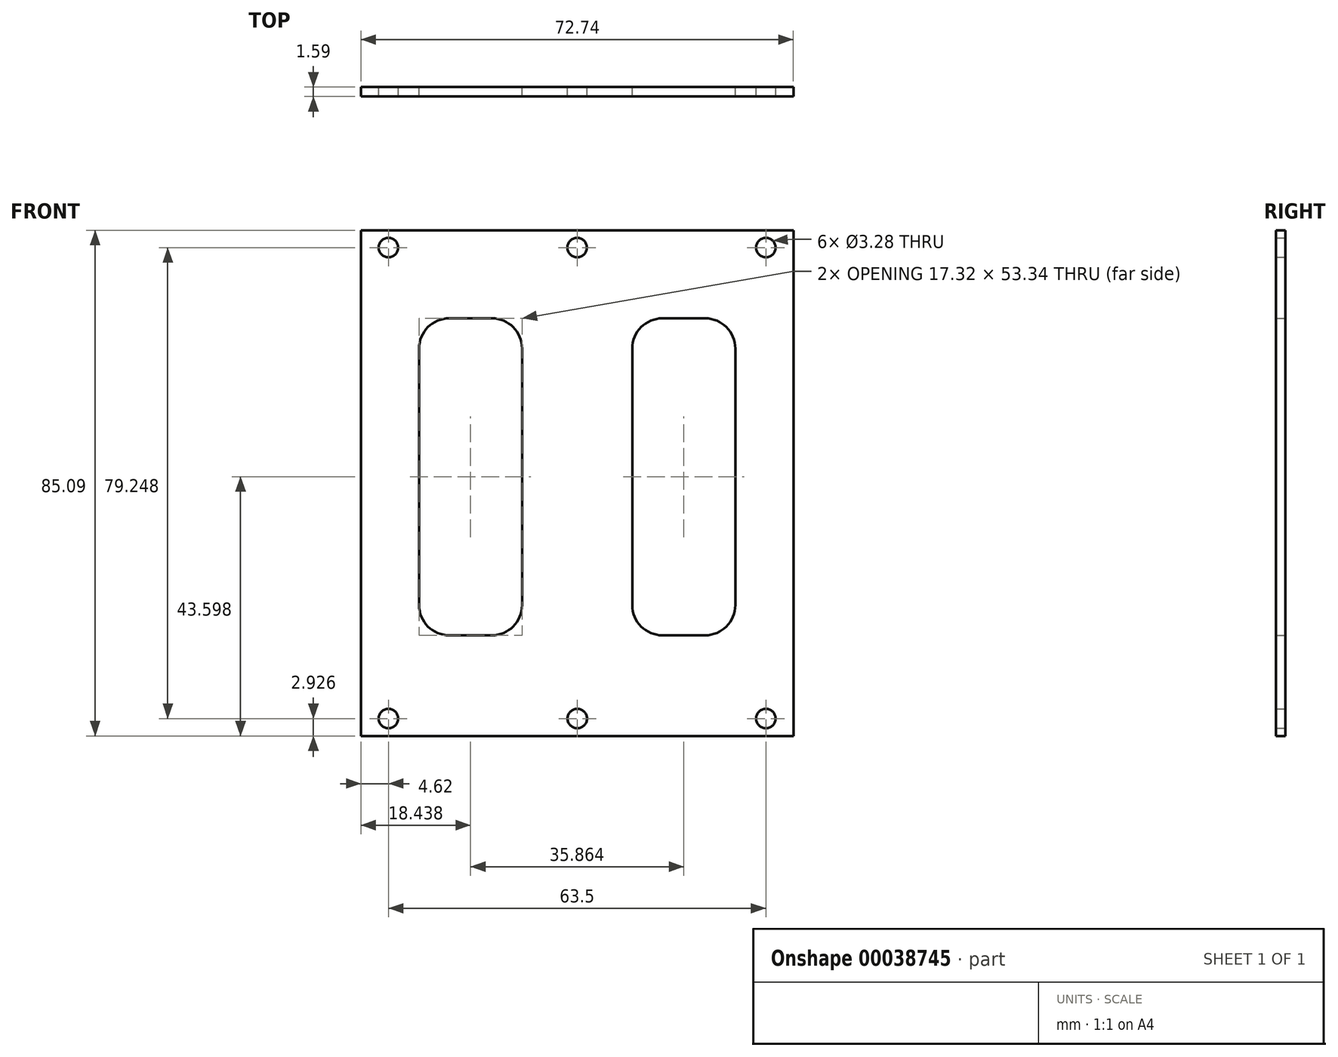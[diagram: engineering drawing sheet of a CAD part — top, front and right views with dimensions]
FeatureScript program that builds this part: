
annotation { "Feature Type Name" : "Feature", "Feature Type Description" : "" }
export const myFeature = defineFeature(function(context is Context, id is Id, definition is map)
    precondition{}
    {
        {
            var Q0;
            Q0=qCreatedBy(makeId("Front.planeOp"),FACE);
            var sketch = newSketch(context, id + "F0", { "sketchPlane" : qUnion([Q0])});
            skLineSegment(sketch, "E0.bottom", {"start": v(-36.37, 49.36) * mm, "end": v(36.37, 49.36) * mm});
            skLineSegment(sketch, "E0.top", {"start": v(-36.37, -35.73) * mm, "end": v(36.37, -35.73) * mm});
            skLineSegment(sketch, "E0.left", {"start": v(-36.37, 49.36) * mm, "end": v(-36.37, -35.73) * mm});
            skLineSegment(sketch, "E0.right", {"start": v(36.37, 49.36) * mm, "end": v(36.37, -35.73) * mm});
            skCircle(sketch, "E1", {"center": v(-31.75, 46.44) * mm, "radius": 1.64 * mm});
            skCircle(sketch, "E2", {"center": v(0, 46.44) * mm, "radius": 1.64 * mm});
            skCircle(sketch, "E3", {"center": v(31.75, 46.44) * mm, "radius": 1.64 * mm});
            skCircle(sketch, "E4", {"center": v(-31.75, -32.8) * mm, "radius": 1.64 * mm});
            skCircle(sketch, "E5", {"center": v(0.02, -32.8) * mm, "radius": 1.64 * mm});
            skCircle(sketch, "E6", {"center": v(31.75, -32.8) * mm, "radius": 1.64 * mm});
            skLineSegment(sketch, "E7", {"start": v(0, 0) * mm, "end": v(0, 63.69) * mm, "construction": true});
            skLineSegment(sketch, "E8", {"start": v(0, 0) * mm, "end": v(0, -66.16) * mm, "construction": true});
            skLineSegment(sketch, "E9.bottom", {"start": v(-26.6, 34.54) * mm, "end": v(-9.27, 34.54) * mm});
            skLineSegment(sketch, "E9.top", {"start": v(-26.6, -18.8) * mm, "end": v(-9.27, -18.8) * mm});
            skLineSegment(sketch, "E9.left", {"start": v(-26.6, 34.54) * mm, "end": v(-26.6, -18.8) * mm});
            skLineSegment(sketch, "E9.right", {"start": v(-9.27, 34.54) * mm, "end": v(-9.27, -18.8) * mm});
            skLineSegment(sketch, "E10.bottom", {"start": v(9.27, 34.54) * mm, "end": v(26.6, 34.54) * mm});
            skLineSegment(sketch, "E10.top", {"start": v(9.27, -18.8) * mm, "end": v(26.6, -18.8) * mm});
            skLineSegment(sketch, "E10.left", {"start": v(9.27, 34.54) * mm, "end": v(9.27, -18.8) * mm});
            skLineSegment(sketch, "E10.right", {"start": v(26.6, 34.54) * mm, "end": v(26.6, -18.8) * mm});
            skSolve(sketch);
        }
        {
            var Q0;
            Q0=makeQuery(id+"F0.imprint","IMPRINT",FACE,{"disambiguationData":[TD([[makeQuery(id+"F0.imprint","IMPRINT",EDGE,{"derivedFrom":sQuery(id+"F0.wireOp",EDGE,"E0.bottom")}),-1.0]])]});
            extrude(context, id + "F1", {"entities" : qUnion([Q0]), "depth" : 1.59 * mm});
        }
        {
            var Q0;
            Q0=makeQuery(id+"F1.opExtrude","SWEPT_EDGE",EDGE,{"disambiguationData":[OSD([sQuery(id+"F0.wireOp",EDGE,"E9.bottom"),sQuery(id+"F0.wireOp",EDGE,"E9.left")])]});
            var Q1;
            Q1=makeQuery(id+"F1.opExtrude","SWEPT_EDGE",EDGE,{"disambiguationData":[OSD([sQuery(id+"F0.wireOp",EDGE,"E9.bottom"),sQuery(id+"F0.wireOp",EDGE,"E9.right")])]});
            var Q2;
            Q2=makeQuery(id+"F1.opExtrude","SWEPT_EDGE",EDGE,{"disambiguationData":[OSD([sQuery(id+"F0.wireOp",EDGE,"E10.top"),sQuery(id+"F0.wireOp",EDGE,"E10.right")])]});
            var Q3;
            Q3=makeQuery(id+"F1.opExtrude","SWEPT_EDGE",EDGE,{"disambiguationData":[OSD([sQuery(id+"F0.wireOp",EDGE,"E10.top"),sQuery(id+"F0.wireOp",EDGE,"E10.left")])]});
            var Q4;
            Q4=makeQuery(id+"F1.opExtrude","SWEPT_EDGE",EDGE,{"disambiguationData":[OSD([sQuery(id+"F0.wireOp",EDGE,"E10.bottom"),sQuery(id+"F0.wireOp",EDGE,"E10.left")])]});
            var Q5;
            Q5=makeQuery(id+"F1.opExtrude","SWEPT_EDGE",EDGE,{"disambiguationData":[OSD([sQuery(id+"F0.wireOp",EDGE,"E10.bottom"),sQuery(id+"F0.wireOp",EDGE,"E10.right")])]});
            var Q6;
            Q6=makeQuery(id+"F1.opExtrude","SWEPT_EDGE",EDGE,{"disambiguationData":[OSD([sQuery(id+"F0.wireOp",EDGE,"E9.top"),sQuery(id+"F0.wireOp",EDGE,"E9.right")])]});
            var Q7;
            Q7=makeQuery(id+"F1.opExtrude","SWEPT_EDGE",EDGE,{"disambiguationData":[OSD([sQuery(id+"F0.wireOp",EDGE,"E9.top"),sQuery(id+"F0.wireOp",EDGE,"E9.left")])]});
            fillet(context, id + "F2", {"entities" : qUnion([Q0, Q1, Q2, Q3, Q4, Q5, Q6, Q7]), "radius" : 5.08 * mm, "tangentPropagation" : true, "allowEdgeOverflow" : false});
        }
    });
